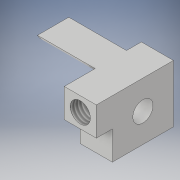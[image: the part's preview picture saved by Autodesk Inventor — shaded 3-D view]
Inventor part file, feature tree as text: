
AUTODESK INVENTOR PART (.ipt)
format: ipt  version: 2019 (Build 230136000, 136)  size: 145,920 bytes
history: native  units: in
note: dims shown in document units (in); Inventor stores cm internally (conversion verified against a paired STEP export)
features: sketch x5, extrude x4, hole x1, thread x1
ambient origin geometry x8: Origin, YZ Plane, XZ Plane, XY Plane, X Axis, Y Axis, Z Axis, Center Point
bodies: Solid1 (feature_tree)
feature tree (11):
  sketch  "Sketch1"  dims[d0=0.4488in d1=0.4764in]
  extrude  "Extrusion1"  Depth=0.4764in
  extrude  "Extrusion2"  Depth=0.1162in
  sketch  "Sketch3"  dims[d2=0.244in d3=0.1162in]
  sketch  "Sketch6"  dims[d4=0.25in d5=0.0in d6=0.45in d7=0.0in]
  hole  "Hole2"  [1 undecoded]
  extrude  "Extrusion8"  Depth=0.4764in
  sketch  "Sketch7"  dims[d19=0.4764in d20=0.2382in]
  extrude  "Extrusion9"  Depth=0.4488in
  thread  "Thread2"  [1 undecoded]
  sketch  "Sketch8"  dims[d29=0.0787in d30=0.4488in d31=0.2244in d33=0.4488in d37=0.1575in d38=0.75in d39=0.119in d40=0.25in d41=0.5635in d42=1.0in d43=0.8108in d46=0.2244in d47=0.125in d48=0.0in d50=0.25in d51=0.2244in d52=0.1122in d53=0.125in d63=0.1122in d64=0.125in d65=0.1575in d66=0.35in d67=0.0in d68=1.0in d69=0.0in d54=1.0in d55=1.0in d56=1.0in d57=0.15in d58=0.25in d59=0.375in d60=0.5635in d61=0.75in d62=0.8108in]
note: 2 required parameter values undecoded (feature->parameter linkage not recoverable at this tier; creation-order binding heuristic only, values carry confidence <= 0.55)
